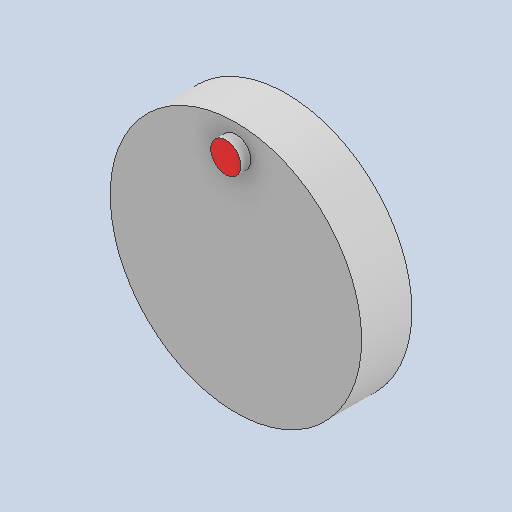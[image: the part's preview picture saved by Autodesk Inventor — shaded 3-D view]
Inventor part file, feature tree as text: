
AUTODESK INVENTOR PART (.ipt)
format: ipt  version: 2022 (Build 260153000, 153)  size: 112,128 bytes
history: native  units: mm
features: extrude x2, sketch x2, other x1
ambient origin geometry x8: Origin, YZ Plane, XZ Plane, XY Plane, X Axis, Y Axis, Z Axis, Center Point
bodies: Body1 (feature_tree)
feature tree (5):
  other  "솔리드1"
  extrude  "돌출1"  Depth=25.0mm
  extrude  "돌출2"  Depth=5.0mm TaperAngle=0.0deg
  sketch  "스케치1"
  sketch  "스케치3"
